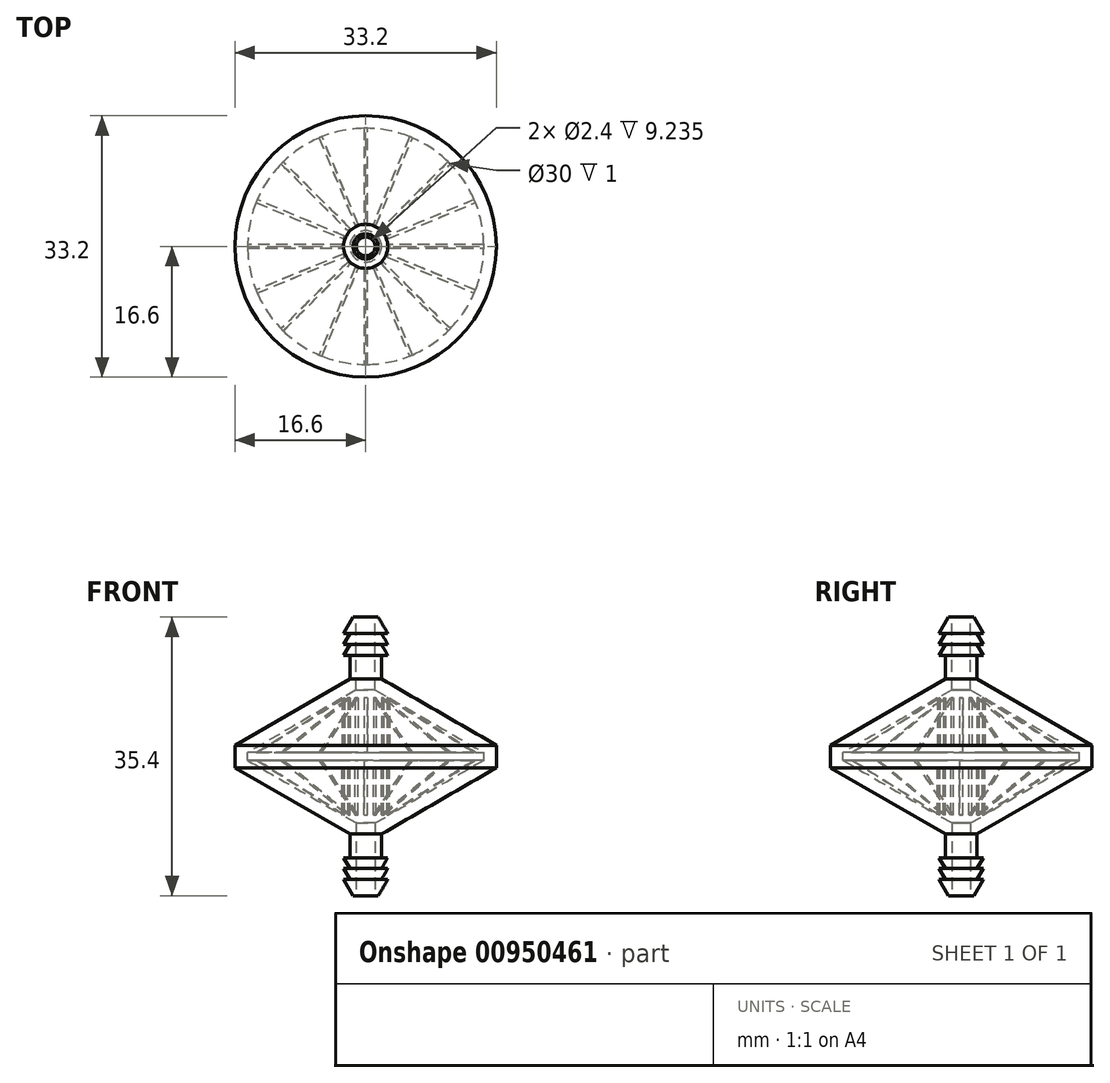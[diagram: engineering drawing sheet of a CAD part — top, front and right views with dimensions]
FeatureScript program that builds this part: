
annotation { "Feature Type Name" : "Feature", "Feature Type Description" : "" }
export const myFeature = defineFeature(function(context is Context, id is Id, definition is map)
    precondition{}
    {
        {
            var Q0;
            Q0=qCreatedBy(makeId("Front.planeOp"),FACE);
            var sketch = newSketch(context, id + "F0", { "sketchPlane" : qUnion([Q0])});
            skLineSegment(sketch, "E0", {"start": v(1.2, 17.7) * mm, "end": v(1.6, 17.7) * mm});
            skLineSegment(sketch, "E1", {"start": v(1.6, 17.7) * mm, "end": v(2.8, 15.62) * mm});
            skLineSegment(sketch, "E2", {"start": v(2.8, 15.62) * mm, "end": v(2, 15.62) * mm});
            skLineSegment(sketch, "E3", {"start": v(2, 15.62) * mm, "end": v(2.8, 14.24) * mm});
            skLineSegment(sketch, "E4", {"start": v(2.8, 14.24) * mm, "end": v(2, 14.24) * mm});
            skLineSegment(sketch, "E5", {"start": v(2, 14.24) * mm, "end": v(2.8, 12.85) * mm});
            skLineSegment(sketch, "E6", {"start": v(2.8, 12.85) * mm, "end": v(2, 12.85) * mm});
            skLineSegment(sketch, "E7", {"start": v(2, 12.85) * mm, "end": v(2, 9.85) * mm});
            skLineSegment(sketch, "E8", {"start": v(1.2, 8.47) * mm, "end": v(1.2, 17.7) * mm});
            skLineSegment(sketch, "E9", {"start": v(0, 11.7) * mm, "end": v(0, -0.67) * mm});
            skLineSegment(sketch, "E10", {"start": v(1.2, 8.47) * mm, "end": v(15, 0.5) * mm});
            skLineSegment(sketch, "E11", {"start": v(15, 0.5) * mm, "end": v(15, 0) * mm});
            skLineSegment(sketch, "E12", {"start": v(15, 0) * mm, "end": v(16.6, 0) * mm});
            skLineSegment(sketch, "E13", {"start": v(16.6, 0) * mm, "end": v(16.6, 1.42) * mm});
            skLineSegment(sketch, "E14", {"start": v(16.6, 1.42) * mm, "end": v(2, 9.85) * mm});
            skSolve(sketch);
        }
        {
            var Q0;
            Q0=makeQuery(id+"F0.imprint","IMPRINT",FACE,{"disambiguationData":[TD([[makeQuery(id+"F0.imprint","IMPRINT",EDGE,{"derivedFrom":sQuery(id+"F0.wireOp",EDGE,"E0")}),-1.0]])]});
            var Q1;
            Q1=sQuery(id+"F0.wireOp",EDGE,"E9");
            revolve(context, id + "F1", {"surfaceOperationType" : NewSurfaceOperationType.NEW, "entities" : qUnion([Q0]), "axis" : qUnion([Q1]), "revolveType" : RevolveType.FULL});
        }
        {
            var Q0;
            Q0=qCreatedBy(makeId("Top.planeOp"),FACE);
            var Q1;
            Q1=makeQuery(id+"F1.opRevolve","SWEPT_FACE",FACE,{"disambiguationData":[OSD([sQuery(id+"F0.wireOp",EDGE,"E12")])]});
            var Q2;
            Q2=makeQuery(id+"F1.opRevolve","SWEPT_FACE",FACE,{"disambiguationData":[OSD([sQuery(id+"F0.wireOp",EDGE,"E12")])]});
            var sketch = newSketch(context, id + "F2", { "sketchPlane" : qUnion([Q0, Q1, Q2])});
            skArc(sketch, "E15.0", {"start": v(-15, 0.2) * mm, "mid": v(-15, 0) * mm, "end": v(-15, -0.2) * mm});
            skLineSegment(sketch, "E16", {"start": v(-15, -0.2) * mm, "end": v(-3, -0.2) * mm});
            skLineSegment(sketch, "E17", {"start": v(-3, -0.2) * mm, "end": v(-3, 0.2) * mm});
            skLineSegment(sketch, "E18", {"start": v(-3, 0.2) * mm, "end": v(-15, 0.2) * mm});
            skSolve(sketch);
        }
        {
            var Q0;
            Q0=makeQuery(id+"F2.imprint","IMPRINT",FACE,{"disambiguationData":[TD([[makeQuery(id+"F2.imprint","IMPRINT",EDGE,{"derivedFrom":sQuery(id+"F2.wireOp",EDGE,"E15.0")}),1.0]])]});
            extrude(context, id + "F3", {"entities" : qUnion([Q0]), "endBound" : BoundingType.UP_TO_NEXT, "depth" : 25 * mm, "offsetDistance" : 25 * mm});
        }
        {
            var Q0;
            Q0=makeQuery(id+"F3.opExtrude","SWEPT_BODY",BODY,{"disambiguationData":[OSD([sQuery(id+"F2.wireOp",EDGE,"E15.0"),sQuery(id+"F2.wireOp",EDGE,"E16"),sQuery(id+"F2.wireOp",EDGE,"E17"),sQuery(id+"F2.wireOp",EDGE,"E18")])]});
            var Q1;
            Q1=sQuery(id+"F0.wireOp",EDGE,"E9");
            circularPattern(context, id + "F4", {"operationType" : NewBodyOperationType.ADD, "entities" : qUnion([Q0]), "axis" : qUnion([Q1]), "angle" : 360 * degree, "instanceCount" : 16, "equalSpace" : true});
        }
        {
            var Q0;
            {var subQ0=sQuery(id+"F2.wireOp",EDGE,"E15.0");Q0=makeQuery(id+"F2.imprint","IMPRINT",FACE,{"disambiguationData":[TD([[makeQuery(id+"F2.imprint","IMPRINT",EDGE,{"derivedFrom":subQ0}),-1.0]])]});}
            var Q1;
            Q1=qCreatedBy(makeId("Top.planeOp"),FACE);
            var sketch = newSketch(context, id + "F5", { "sketchPlane" : qUnion([Q0, Q1])});
            skCircle(sketch, "E19", {"center": v(0, 0) * mm, "radius": 15 * mm});
            skSolve(sketch);
        }
        {
            var Q0;
            {var subQ0=sQuery(id+"F5.wireOp",EDGE,"E19");var subQ1=makeQuery(id+"F5.imprint","IMPRINT",VERTEX,{"disambiguationData":[OD(0.0)],"derivedFrom":subQ0});Q0=makeQuery(id+"F5.imprint","IMPRINT",FACE,{"disambiguationData":[TD([[makeQuery(id+"F5.imprint","IMPRINT",EDGE,{"disambiguationData":[TD([[subQ1,-1.0]])],"derivedFrom":subQ0}),1.0]])]});}
            extrude(context, id + "F6", {"entities" : qUnion([Q0]), "operationType" : NewBodyOperationType.REMOVE, "depth" : 0.5 * mm, "offsetDistance" : 25 * mm});
        }
        {
            var Q0;
            Q0=makeQuery(id+"F1.opRevolve","SWEPT_BODY",BODY,{"disambiguationData":[OSD([sQuery(id+"F0.wireOp",EDGE,"E0"),sQuery(id+"F0.wireOp",EDGE,"E1"),sQuery(id+"F0.wireOp",EDGE,"E2"),sQuery(id+"F0.wireOp",EDGE,"E3"),sQuery(id+"F0.wireOp",EDGE,"E4"),sQuery(id+"F0.wireOp",EDGE,"E5"),sQuery(id+"F0.wireOp",EDGE,"E6"),sQuery(id+"F0.wireOp",EDGE,"E7"),sQuery(id+"F0.wireOp",EDGE,"E8"),sQuery(id+"F0.wireOp",EDGE,"E10"),sQuery(id+"F0.wireOp",EDGE,"E11"),sQuery(id+"F0.wireOp",EDGE,"E12"),sQuery(id+"F0.wireOp",EDGE,"E13"),sQuery(id+"F0.wireOp",EDGE,"E14")])]});
            var Q1;
            Q1=qCreatedBy(makeId("Top.planeOp"),FACE);
            mirror(context, id + "F7", {"operationType" : NewBodyOperationType.ADD, "entities" : qUnion([Q0]), "mirrorPlane" : qUnion([Q1])});
        }
    });
